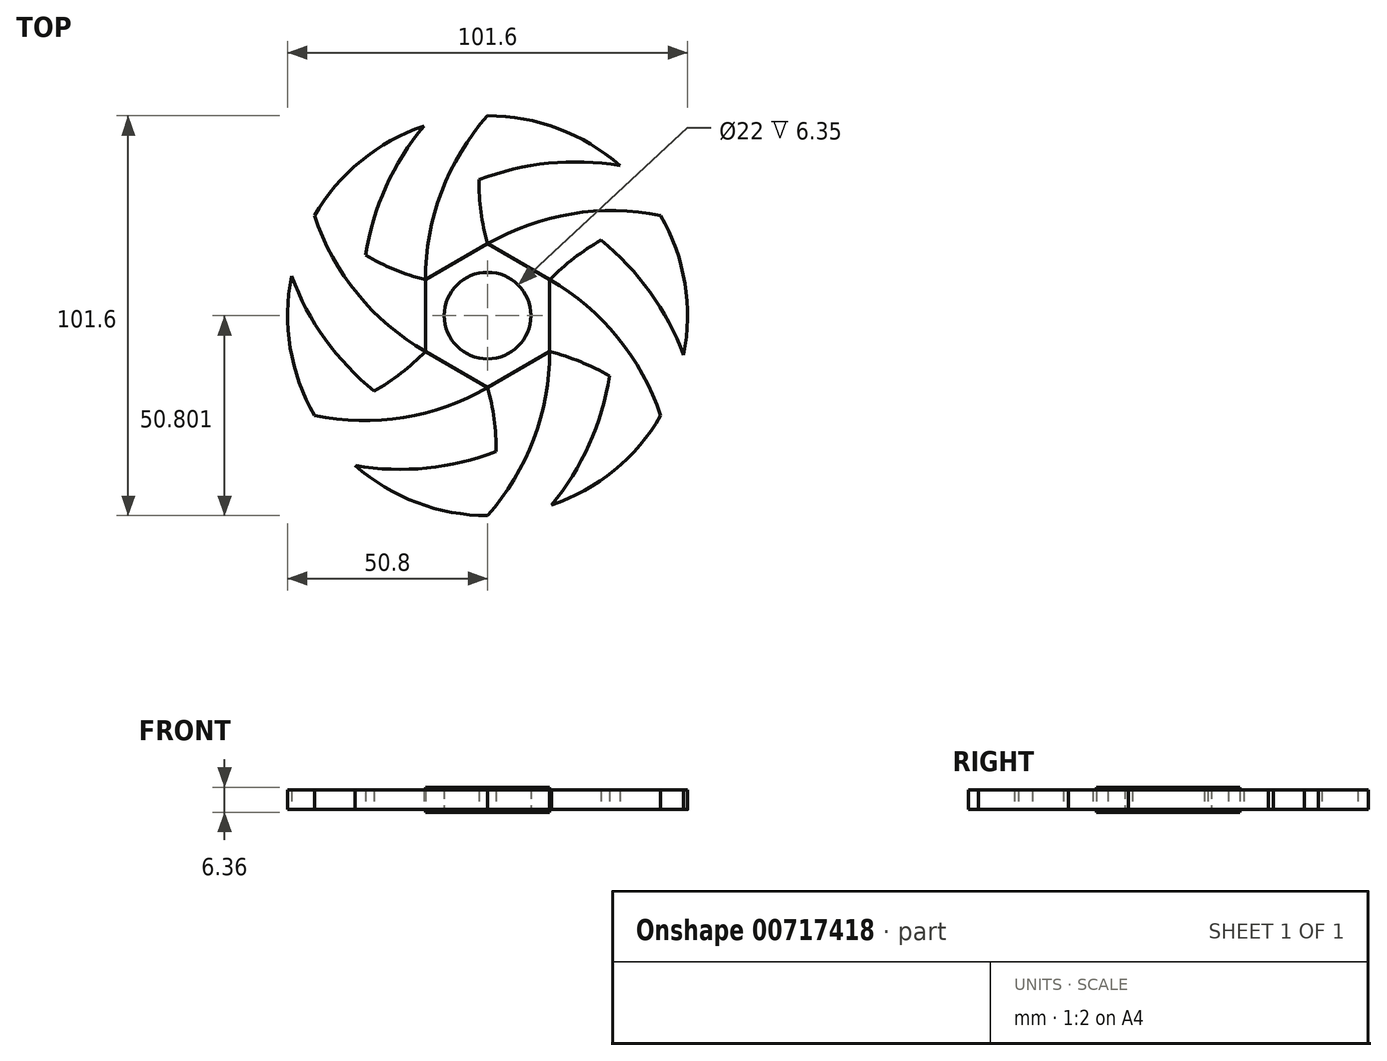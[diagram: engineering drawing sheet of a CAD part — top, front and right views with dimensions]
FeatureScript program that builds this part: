
annotation { "Feature Type Name" : "Feature", "Feature Type Description" : "" }
export const myFeature = defineFeature(function(context is Context, id is Id, definition is map)
    precondition{}
    {
        {
            var Q0;
            Q0=qCreatedBy(makeId("Top.planeOp"),FACE);
            var sketch = newSketch(context, id + "F0", { "sketchPlane" : qUnion([Q0])});
            skCircle(sketch, "E0", {"center": v(-5.22, -5.4) * mm, "radius": 11 * mm});
            skPoint(sketch, "E1.0.midPoint", {"position": v(40.05, 19.72) * mm});
            skLineSegment(sketch, "E2", {"start": v(-5.22, -5.4) * mm, "end": v(-21.03, -5.4) * mm, "construction": true});
            skLineSegment(sketch, "E3", {"start": v(-5.22, -5.4) * mm, "end": v(-5.22, 10.67) * mm, "construction": true});
            skLineSegment(sketch, "E4", {"start": v(-5.22, -5.4) * mm, "end": v(10.59, -5.4) * mm, "construction": true});
            skLineSegment(sketch, "E5", {"start": v(-5.22, -5.4) * mm, "end": v(-5.22, -21.49) * mm, "construction": true});
            skCircle(sketch, "E6.cCircle", {"center": v(-5.22, -5.4) * mm, "radius": 15.8 * mm, "construction": true});
            skLineSegment(sketch, "E6.0", {"start": v(10.59, 3.72) * mm, "end": v(10.59, -14.54) * mm});
            skLineSegment(sketch, "E6.1", {"start": v(10.59, -14.54) * mm, "end": v(-5.22, -23.66) * mm});
            skLineSegment(sketch, "E6.2", {"start": v(-5.22, -23.66) * mm, "end": v(-21.03, -14.54) * mm});
            skLineSegment(sketch, "E6.3", {"start": v(-21.03, -14.54) * mm, "end": v(-21.03, 3.72) * mm});
            skLineSegment(sketch, "E6.4", {"start": v(-21.03, 3.72) * mm, "end": v(-5.22, 12.84) * mm});
            skLineSegment(sketch, "E6.5", {"start": v(-5.22, 12.84) * mm, "end": v(10.59, 3.72) * mm});
            skPoint(sketch, "E6.0.midPoint", {"position": v(10.59, -5.4) * mm});
            skCircle(sketch, "E7.cCircle", {"center": v(-5.22, -5.4) * mm, "radius": 44 * mm, "construction": true});
            skLineSegment(sketch, "E7.0", {"start": v(-5.22, 45.4) * mm, "end": v(38.77, 20) * mm, "construction": true});
            skLineSegment(sketch, "E7.1", {"start": v(38.77, 20) * mm, "end": v(38.77, -30.8) * mm, "construction": true});
            skLineSegment(sketch, "E7.2", {"start": v(38.77, -30.8) * mm, "end": v(-5.22, -56.2) * mm, "construction": true});
            skLineSegment(sketch, "E7.3", {"start": v(-5.22, -56.2) * mm, "end": v(-49.21, -30.8) * mm, "construction": true});
            skLineSegment(sketch, "E7.4", {"start": v(-49.21, -30.8) * mm, "end": v(-49.21, 20) * mm, "construction": true});
            skLineSegment(sketch, "E7.5", {"start": v(-49.21, 20) * mm, "end": v(-5.22, 45.4) * mm, "construction": true});
            skPoint(sketch, "E7.0.midPoint", {"position": v(16.78, 32.7) * mm});
            skArc(sketch, "E8", {"start": v(-5.22, 45.4) * mm, "mid": v(-16.94, 26) * mm, "end": v(-21.03, 3.72) * mm});
            skArc(sketch, "E9", {"start": v(-5.22, 45.4) * mm, "mid": v(-7.43, 29.12) * mm, "end": v(-5.22, 12.84) * mm});
            skArc(sketch, "E10", {"start": v(38.77, -30.8) * mm, "mid": v(27.84, -10.96) * mm, "end": v(10.59, 3.72) * mm});
            skArc(sketch, "E11", {"start": v(38.77, -30.8) * mm, "mid": v(25.79, -20.76) * mm, "end": v(10.59, -14.54) * mm});
            skArc(sketch, "E12", {"start": v(-5.22, -56.2) * mm, "mid": v(6.5, -36.82) * mm, "end": v(10.59, -14.54) * mm});
            skArc(sketch, "E13", {"start": v(-5.22, -56.2) * mm, "mid": v(-3, -39.94) * mm, "end": v(-5.22, -23.66) * mm});
            skArc(sketch, "E14", {"start": v(-49.21, -30.8) * mm, "mid": v(-26.56, -31.27) * mm, "end": v(-5.22, -23.66) * mm});
            skArc(sketch, "E15", {"start": v(-49.21, -30.8) * mm, "mid": v(-34.01, -24.59) * mm, "end": v(-21.03, -14.54) * mm});
            skArc(sketch, "E16", {"start": v(-49.21, 20) * mm, "mid": v(-38.28, 0.14) * mm, "end": v(-21.03, -14.54) * mm});
            skArc(sketch, "E17", {"start": v(-49.21, 20) * mm, "mid": v(-36.23, 9.94) * mm, "end": v(-21.03, 3.72) * mm});
            skArc(sketch, "E18", {"start": v(-38.82, -43.5) * mm, "mid": v(-20.67, -44.13) * mm, "end": v(-3, -39.94) * mm});
            skPoint(sketch, "E18.startSnap0", {"position": v(-27.22, -43.5) * mm});
            skArc(sketch, "E19", {"start": v(-38.82, -43.5) * mm, "mid": v(-23.18, -52.93) * mm, "end": v(-5.22, -56.2) * mm});
            skArc(sketch, "E20.1.0", {"start": v(10.98, -53.56) * mm, "mid": v(20.59, -38.15) * mm, "end": v(25.79, -20.76) * mm});
            skArc(sketch, "E20.1.1", {"start": v(10.98, -53.56) * mm, "mid": v(26.95, -44.72) * mm, "end": v(38.77, -30.8) * mm});
            skArc(sketch, "E20.2.0", {"start": v(44.58, -15.46) * mm, "mid": v(36.04, 0.57) * mm, "end": v(23.57, 13.77) * mm});
            skArc(sketch, "E20.2.1", {"start": v(44.58, -15.46) * mm, "mid": v(44.91, 2.8) * mm, "end": v(38.77, 20) * mm});
            skArc(sketch, "E20.2.2", {"start": v(38.77, 20) * mm, "mid": v(23.57, 13.77) * mm, "end": v(10.59, 3.72) * mm});
            skArc(sketch, "E20.3.0", {"start": v(28.38, 32.7) * mm, "mid": v(10.23, 33.31) * mm, "end": v(-7.43, 29.12) * mm});
            skArc(sketch, "E20.3.1", {"start": v(28.38, 32.7) * mm, "mid": v(12.74, 42.1) * mm, "end": v(-5.22, 45.4) * mm});
            skArc(sketch, "E20.4.0", {"start": v(-21.41, 42.74) * mm, "mid": v(-31.03, 27.34) * mm, "end": v(-36.23, 9.94) * mm});
            skArc(sketch, "E20.4.1", {"start": v(-21.41, 42.74) * mm, "mid": v(-37.4, 33.9) * mm, "end": v(-49.21, 20) * mm});
            skArc(sketch, "E20.5.0", {"start": v(-55.02, 4.64) * mm, "mid": v(-46.48, -11.39) * mm, "end": v(-34.01, -24.59) * mm});
            skArc(sketch, "E20.5.1", {"start": v(-55.02, 4.64) * mm, "mid": v(-55.35, -13.61) * mm, "end": v(-49.21, -30.8) * mm});
            skCircle(sketch, "E21", {"center": v(-5.22, -5.4) * mm, "radius": 50.8 * mm, "construction": true});
            skCircle(sketch, "E22", {"center": v(-5.22, -5.4) * mm, "radius": 4 * mm});
            skArc(sketch, "E23.2.0", {"start": v(38.77, 20) * mm, "mid": v(16.12, 20.45) * mm, "end": v(-5.22, 12.84) * mm});
            skSolve(sketch);
        }
        {
            var Q0;
            Q0=qSketchRegion(id+"F0",true);
            extrude(context, id + "F1", {"entities" : qUnion([Q0]), "endBound" : BoundingType.SYMMETRIC, "depth" : 5 * mm, "offsetDistance" : 25.4 * mm});
        }
        {
            var Q0;
            Q0=makeQuery(id+"F0.imprint","IMPRINT",FACE,{"disambiguationData":[TD([[makeQuery(id+"F0.imprint","IMPRINT",EDGE,{"derivedFrom":sQuery(id+"F0.wireOp",EDGE,"E0")}),-1.0]])]});
            extrude(context, id + "F2", {"entities" : qUnion([Q0]), "operationType" : NewBodyOperationType.ADD, "endBound" : BoundingType.SYMMETRIC, "depth" : 6.35 * mm, "offsetDistance" : 25.4 * mm});
        }
    });
